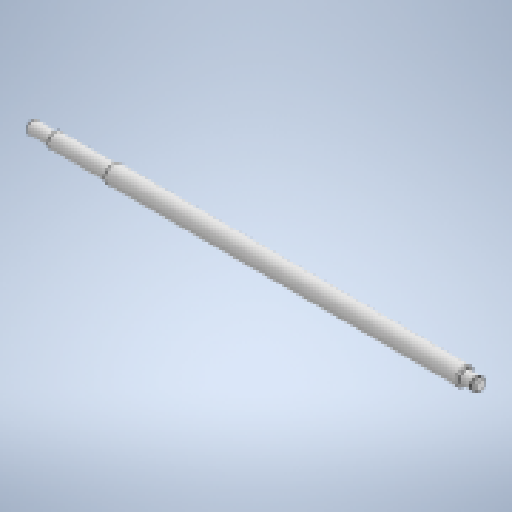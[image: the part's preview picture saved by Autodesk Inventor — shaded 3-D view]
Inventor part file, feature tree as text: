
AUTODESK INVENTOR PART (.ipt)
format: ipt  version: 2023 (Build 270158000, 158)  size: 167,424 bytes
history: native  units: in
note: dims shown in document units (in); Inventor stores cm internally (conversion verified against a paired STEP export)
features: revolve x1, sketch x1
ambient origin geometry x8: Origin, YZ Plane, XZ Plane, XY Plane, X Axis, Y Axis, Z Axis, Center Point
bodies: Solid1 (feature_tree)
feature tree (2):
  revolve  "Revolution1"  [1 undecoded]
  sketch  "Sketch1"  dims[d0=0.1575in d1=0.1969in d2=0.2362in d3=135.0deg d4=135.0deg d5=0.5906in d6=1.5354in d7=135.0deg d8=0.1575in d9=0.2756in d10=0.3937in d11=0.0079in d12=0.0354in d14=135.0deg d15=11.811in d16=90.0deg]
note: 1 required parameter value undecoded (feature->parameter linkage not recoverable at this tier; creation-order binding heuristic only, values carry confidence <= 0.55)
